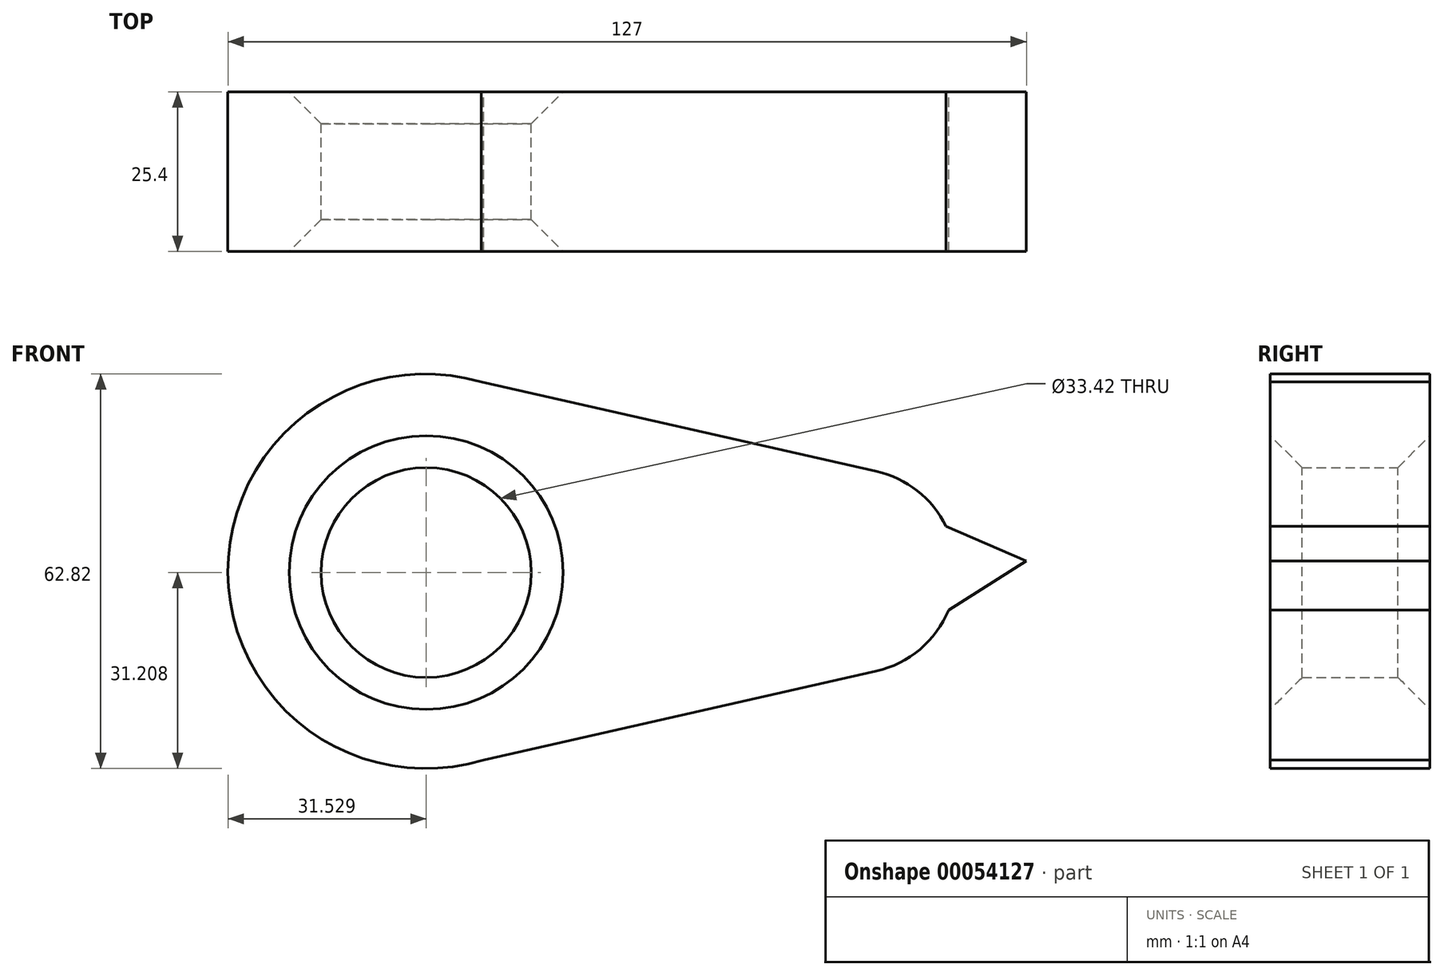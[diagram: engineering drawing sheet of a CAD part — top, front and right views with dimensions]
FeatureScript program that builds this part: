
annotation { "Feature Type Name" : "Feature", "Feature Type Description" : "" }
export const myFeature = defineFeature(function(context is Context, id is Id, definition is map)
    precondition{}
    {
        {
            var Q0;
            Q0=qCreatedBy(makeId("Front.planeOp"),FACE);
            var sketch = newSketch(context, id + "F0", { "sketchPlane" : qUnion([Q0])});
            skCircle(sketch, "E0", {"center": v(-33.76, 17.78) * mm, "radius": 31.41 * mm});
            skCircle(sketch, "E1", {"center": v(34.36, 17.8) * mm, "radius": 16.31 * mm});
            skLineSegment(sketch, "E2", {"start": v(-24.85, 47.9) * mm, "end": v(37.96, 33.7) * mm});
            skLineSegment(sketch, "E3", {"start": v(37.96, 1.88) * mm, "end": v(-24.52, -12.24) * mm});
            skCircle(sketch, "E4", {"center": v(-33.64, 17.58) * mm, "radius": 16.7 * mm});
            skLineSegment(sketch, "E5", {"start": v(49.02, 24.94) * mm, "end": v(61.83, 19.4) * mm});
            skLineSegment(sketch, "E6", {"start": v(49.46, 11.62) * mm, "end": v(61.83, 19.4) * mm});
            skSolve(sketch);
        }
        {
            var Q0;
            Q0 = qSketchRegion(id + "F0", true);
            extrude(context, id + "F1", {"entities" : qUnion([Q0]), "depth" : 25.4 * mm});
        }
        {
            var Q0;
            Q0=makeQuery(id+"F1.opExtrude","CAP_EDGE",EDGE,{"disambiguationData":[OSD([sQuery(id+"F0.wireOp",EDGE,"E4")])],"isStart":false});
            chamfer(context, id + "F2", {"entities" : qUnion([Q0]), "width" : 5.08 * mm, "tangentPropagation" : true});
        }
        {
            var Q0;
            Q0=makeQuery(id+"F1.opExtrude","CAP_EDGE",EDGE,{"disambiguationData":[OSD([sQuery(id+"F0.wireOp",EDGE,"E4")])],"isStart":true});
            chamfer(context, id + "F3", {"entities" : qUnion([Q0]), "width" : 5.08 * mm, "tangentPropagation" : true});
        }
    });
